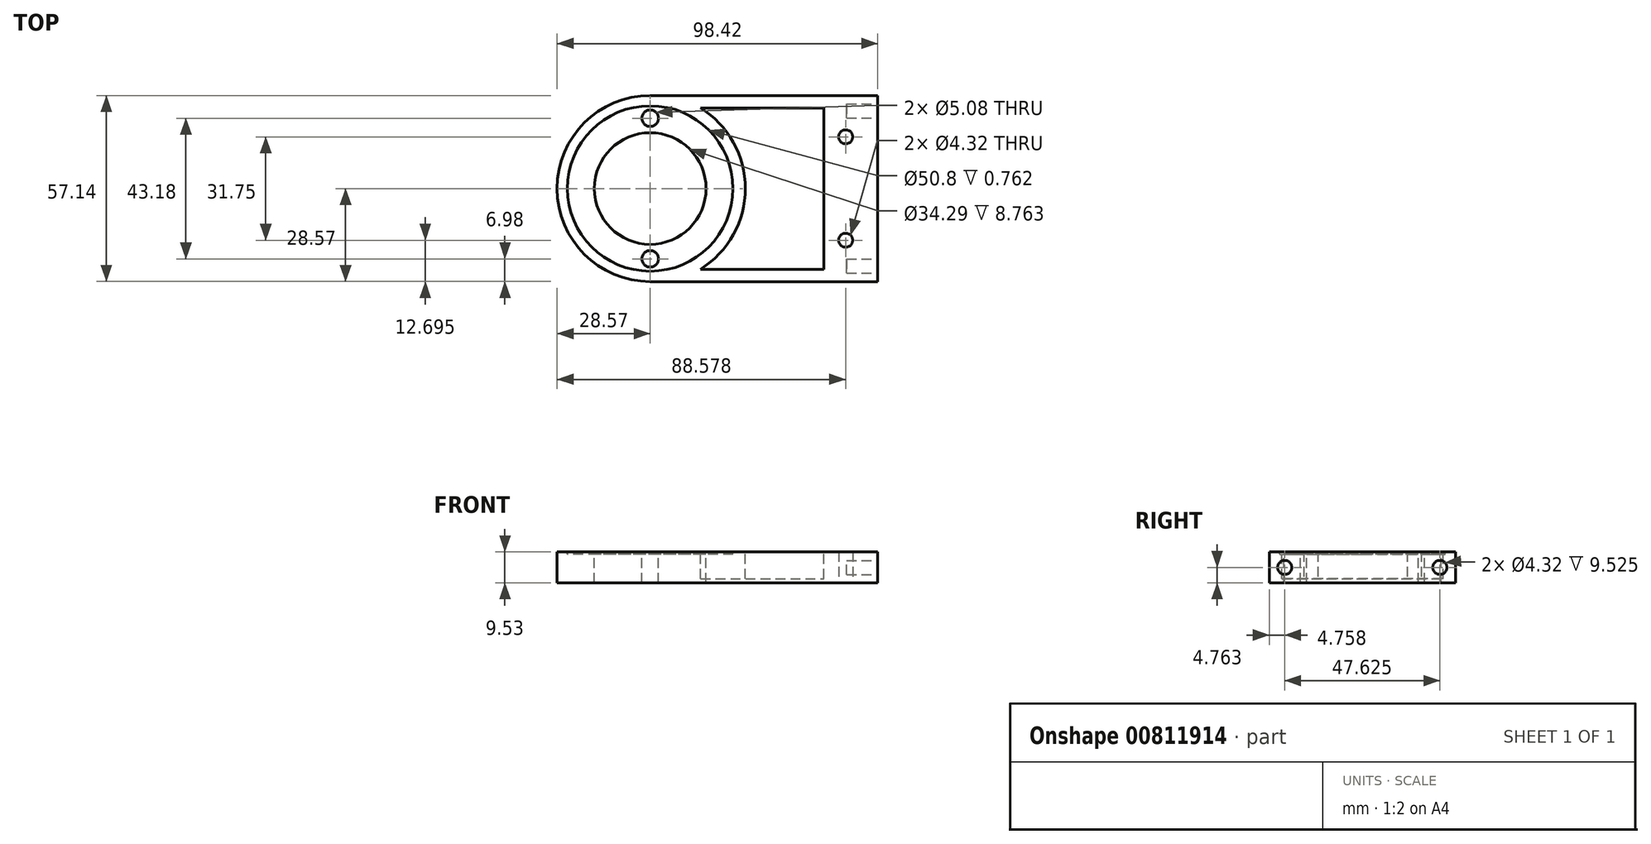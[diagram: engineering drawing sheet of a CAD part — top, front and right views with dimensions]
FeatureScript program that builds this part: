
annotation { "Feature Type Name" : "Feature", "Feature Type Description" : "" }
export const myFeature = defineFeature(function(context is Context, id is Id, definition is map)
    precondition{}
    {
        {
            var Q0;
            Q0=qCreatedBy(makeId("Top.planeOp"),FACE);
            var sketch = newSketch(context, id + "F0", { "sketchPlane" : qUnion([Q0])});
            skCircle(sketch, "E0", {"center": v(0, 0) * mm, "radius": 28.58 * mm});
            skLineSegment(sketch, "E1.bottom", {"start": v(0, 28.58) * mm, "end": v(69.85, 28.58) * mm});
            skLineSegment(sketch, "E1.top", {"start": v(0, -28.58) * mm, "end": v(69.85, -28.58) * mm});
            skLineSegment(sketch, "E1.left", {"start": v(0, 28.58) * mm, "end": v(0, -28.58) * mm});
            skLineSegment(sketch, "E1.right", {"start": v(69.85, 28.58) * mm, "end": v(69.85, -28.58) * mm});
            skSolve(sketch);
        }
        {
            var Q0;
            {var subQ0=sQuery(id+"F0.wireOp",EDGE,"E1.left");var subQ1=makeQuery(id+"F0.imprint","IMPRINT",EDGE,{"derivedFrom":subQ0});var subQ5=sQuery(id+"F0.wireOp",EDGE,"E1.bottom");Q0=qUnion([makeQuery(id+"F0.imprint","IMPRINT",FACE,{"disambiguationData":[TD([[subQ1,-1.0]])]}),makeQuery(id+"F0.imprint","IMPRINT",FACE,{"disambiguationData":[TD([[makeQuery(id+"F0.imprint","IMPRINT",EDGE,{"derivedFrom":subQ5}),-1.0]])]}),makeQuery(id+"F0.imprint","IMPRINT",FACE,{"disambiguationData":[TD([[subQ1,1.0]])]})]);}
            extrude(context, id + "F1", {"entities" : qUnion([Q0]), "depth" : 9.52 * mm});
        }
        {
            var Q0;
            Q0=makeQuery(id+"F1.opExtrude","CAP_FACE",FACE,{"disambiguationData":[OSD([sQuery(id+"F0.wireOp",EDGE,"E0"),sQuery(id+"F0.wireOp",EDGE,"E1.bottom"),sQuery(id+"F0.wireOp",EDGE,"E1.top"),sQuery(id+"F0.wireOp",EDGE,"E1.right")])],"isStart":false});
            var sketch = newSketch(context, id + "F2", { "sketchPlane" : qUnion([Q0])});
            skCircle(sketch, "E2", {"center": v(0, 0) * mm, "radius": 25.4 * mm});
            skPoint(sketch, "E3.visualSharp", {"position": v(63.5, 25.4) * mm});
            skPoint(sketch, "E4.visualSharp", {"position": v(63.5, -25.4) * mm});
            skSolve(sketch);
        }
        {
            var Q0;
            Q0=makeQuery(id+"F2.imprint","IMPRINT",FACE,{"disambiguationData":[TD([[makeQuery(id+"F2.imprint","IMPRINT",EDGE,{"derivedFrom":sQuery(id+"F2.wireOp",EDGE,"E2")}),1.0]])]});
            extrude(context, id + "F3", {"entities" : qUnion([Q0]), "operationType" : NewBodyOperationType.REMOVE, "oppositeDirection" : true, "depth" : 0.76 * mm});
        }
        {
            var Q0;
            Q0=makeQuery(id+"F3.boolean.opBoolean","COPY",FACE,{"derivedFrom":makeQuery(id+"F3.opExtrude","CAP_FACE",FACE,{"disambiguationData":[OSD([sQuery(id+"F2.wireOp",EDGE,"E2")])],"isStart":false})});
            var sketch = newSketch(context, id + "F4", { "sketchPlane" : qUnion([Q0])});
            skCircle(sketch, "E5", {"center": v(0, 0) * mm, "radius": 17.15 * mm});
            skCircle(sketch, "E6", {"center": v(0, 0) * mm, "radius": 21.59 * mm, "construction": true});
            skCircle(sketch, "E7", {"center": v(0, 21.59) * mm, "radius": 2.54 * mm});
            skCircle(sketch, "E8", {"center": v(0, -21.59) * mm, "radius": 2.54 * mm});
            skSolve(sketch);
        }
        {
            var Q0;
            {Q0=qUnion([makeQuery(id+"F4.imprint","IMPRINT",FACE,{"disambiguationData":[TD([[makeQuery(id+"F4.imprint","IMPRINT",EDGE,{"derivedFrom":sQuery(id+"F4.wireOp",EDGE,"E5")}),1.0]])]}),makeQuery(id+"F4.imprint","IMPRINT",FACE,{"disambiguationData":[TD([[makeQuery(id+"F4.imprint","IMPRINT",EDGE,{"derivedFrom":sQuery(id+"F4.wireOp",EDGE,"E7")}),1.0]])]}),makeQuery(id+"F4.imprint","IMPRINT",FACE,{"disambiguationData":[TD([[makeQuery(id+"F4.imprint","IMPRINT",EDGE,{"derivedFrom":sQuery(id+"F4.wireOp",EDGE,"E8")}),1.0]])]})]);}
            extrude(context, id + "F5", {"entities" : qUnion([Q0]), "operationType" : NewBodyOperationType.REMOVE, "endBound" : BoundingType.THROUGH_ALL, "oppositeDirection" : true, "depth" : 25.4 * mm});
        }
        {
            var Q0;
            Q0=makeQuery(id+"F1.opExtrude","CAP_FACE",FACE,{"disambiguationData":[OSD([sQuery(id+"F0.wireOp",EDGE,"E0"),sQuery(id+"F0.wireOp",EDGE,"E1.bottom"),sQuery(id+"F0.wireOp",EDGE,"E1.top"),sQuery(id+"F0.wireOp",EDGE,"E1.right")])],"isStart":true});
            var sketch = newSketch(context, id + "F6", { "sketchPlane" : qUnion([Q0])});
            skCircle(sketch, "E9", {"center": v(60, 15.88) * mm, "radius": 2.16 * mm});
            skCircle(sketch, "E10", {"center": v(60, -15.88) * mm, "radius": 2.16 * mm});
            skSolve(sketch);
        }
        {
            var Q0;
            {Q0=qUnion([makeQuery(id+"F6.imprint","IMPRINT",FACE,{"disambiguationData":[TD([[makeQuery(id+"F6.imprint","IMPRINT",EDGE,{"derivedFrom":sQuery(id+"F6.wireOp",EDGE,"E9")}),1.0]])]}),makeQuery(id+"F6.imprint","IMPRINT",FACE,{"disambiguationData":[TD([[makeQuery(id+"F6.imprint","IMPRINT",EDGE,{"derivedFrom":sQuery(id+"F6.wireOp",EDGE,"E10")}),1.0]])]})]);}
            extrude(context, id + "F7", {"entities" : qUnion([Q0]), "operationType" : NewBodyOperationType.REMOVE, "endBound" : BoundingType.THROUGH_ALL, "oppositeDirection" : true, "depth" : 25.4 * mm});
        }
        {
            var Q0;
            Q0=makeQuery(id+"F1.opExtrude","SWEPT_FACE",FACE,{"disambiguationData":[OSD([sQuery(id+"F0.wireOp",EDGE,"E1.right")])]});
            var sketch = newSketch(context, id + "F8", { "sketchPlane" : qUnion([Q0])});
            skCircle(sketch, "E11", {"center": v(-23.81, 4.76) * mm, "radius": 2.16 * mm});
            skCircle(sketch, "E12", {"center": v(23.81, 4.76) * mm, "radius": 2.16 * mm});
            skSolve(sketch);
        }
        {
            var Q0;
            {Q0=qUnion([makeQuery(id+"F8.imprint","IMPRINT",FACE,{"disambiguationData":[TD([[makeQuery(id+"F8.imprint","IMPRINT",EDGE,{"derivedFrom":sQuery(id+"F8.wireOp",EDGE,"E11")}),1.0]])]}),makeQuery(id+"F8.imprint","IMPRINT",FACE,{"disambiguationData":[TD([[makeQuery(id+"F8.imprint","IMPRINT",EDGE,{"derivedFrom":sQuery(id+"F8.wireOp",EDGE,"E12")}),1.0]])]})]);}
            extrude(context, id + "F9", {"entities" : qUnion([Q0]), "operationType" : NewBodyOperationType.REMOVE, "oppositeDirection" : true, "depth" : 9.52 * mm});
        }
        {
            var Q0;
            Q0=makeQuery(id+"F1.opExtrude","CAP_FACE",FACE,{"disambiguationData":[OSD([sQuery(id+"F0.wireOp",EDGE,"E0"),sQuery(id+"F0.wireOp",EDGE,"E1.bottom"),sQuery(id+"F0.wireOp",EDGE,"E1.top"),sQuery(id+"F0.wireOp",EDGE,"E1.right")])],"isStart":false});
            var sketch = newSketch(context, id + "F10", { "sketchPlane" : qUnion([Q0])});
            skArc(sketch, "E13.0", {"start": v(15.49, -24.77) * mm, "mid": v(29.21, 0) * mm, "end": v(15.49, 24.77) * mm});
            skLineSegment(sketch, "E14.0", {"start": v(15.49, 24.77) * mm, "end": v(53.34, 24.77) * mm});
            skLineSegment(sketch, "E15.0", {"start": v(15.49, -24.77) * mm, "end": v(53.34, -24.77) * mm});
            skLineSegment(sketch, "E16.0", {"start": v(53.34, 24.77) * mm, "end": v(53.34, -24.77) * mm});
            skSolve(sketch);
        }
        {
            var Q0;
            Q0=qSketchRegion(id+"F10",true);
            extrude(context, id + "F11", {"entities" : qUnion([Q0]), "operationType" : NewBodyOperationType.REMOVE, "oppositeDirection" : true, "depth" : 8.25 * mm});
        }
    });
